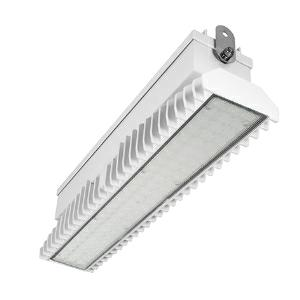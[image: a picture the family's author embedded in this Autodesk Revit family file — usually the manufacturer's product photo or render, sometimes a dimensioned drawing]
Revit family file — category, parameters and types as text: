
# Revit family: 3f_filippi_-_3f_lem_ampio_3f_filippi_-_58899_a0812_-_3f_lem_1_led_50_dali_cr_ampio___vs_c1d0
name_source: partatom
category: Lighting Fixtures
units: mm (PartAtom-declared; Revit-internal decimal feet)

## family parameters
Cut with Voids When Loaded = No
Host = Face
Light Source = No
Part Type = Normal
Room Calculation Point = No
Round Connector Dimension = Use Diameter
Shared = No

## types (1)
- 3F Filippi - 3F LEM Ampio (1 x LED, 6652 lm, 56 W, 4000 K)
    Apparent Load = 56 VA
    Approval mark = CE
    CIE Flux Codes = 67 90 97 100 100
    Color Rendering = 80
    Color Temperature = 4000 K
    Control Gear = Electronic transformer
    Default Elevation = 1800 mm
    Description = Industrial luminaire with high light output and high luminous efficiency designed with the most innovative technologies for environments with temperature up to 55°C.

ILLUMINOTECHNICAL
Luminous efficiency 100% (DLOR 98%, ULOR 2%).
Initial luminous flux of the luminaire 6652 lm.
Direct symmetric wide distribution: the illuminated area has a rectangular shape.
Installation Interdistance Transv.D = 1.24 x hu - Long.D = 1.20 x hu.
Tabular UGR (CIE 117 - 4H-8H; S=0.25H; 70/50/20): RUG 25.9 - 25.7.
Beam angle: 82° - 83°.
Luminous efficacy 119 lm/W.
Lifetime (L93/B10): 30000 h. (tq+25°C)
Lifetime (L90/B10): 50000 h. (tq+25°C)
Lifetime (L85/B10): 80000 h. (tq+25°C)
Lifetime (L80/B10): 100000 h. (tq+25°C)
Lifetime (L85/B10): 50000 h. (tq+55°C)
Sudden decreased luminous flux after 50000 hours: 0% (C0).
Photobiological safety in compliance with IEC/TR 62778: RG0 risk exempt, (IEC 62471).
In compliance with IEC/EN 62722-2-1 - IEC/EN 62717 standards.

SOURCE
Mid-Power linear LED module 50W/840.
Energy efficiency class (UE 2019/2020 - UE 2019/2015): C.
CIE 13.3 Colour rendering index: CRI >80 (R9 <50%).
IES TM-30 Fidelity Index: Rf = 84 Rg = 95.
CCT nominal colour temperature 4000 K.
Colour initial tolerance (MacAdam): SDCM 3.

MECHANICAL
Passive modular heatsinks in die-casted aluminium, painted in white colour.
To optimize the thermal management of the LED module, the heatsinks are oversized and provided with self-cleaning of cooling fins.
Wiring body in aluminium and galvanised steel anchored solidly to the sinks and thermally separated.
3F Lens lenses with high luminous efficiency, transparent methacrylate (PMMA), fixed to the LED modules.
Fixing brackets in stainless steel.
Luminaire with limited surface temperature. - D - (EN 60598-2-24)
Dimensions: 542x115 mm, height 154 mm. Weight 6.76 kg.
IP65 protection degree.
Mechanical strength to impacts IK06 (1 joule).
Glow-wire test resistance 650°C.

ELECTRICAL
Halogen Free DALI-2 DATI (Parts 251, 252, 253), PUSH-DIM, electronic wiring 230V-50/60Hz, power factor 0.95 at full load, THD <25%, constant output current, class I, 1 driver, 1 DALI addresse.
Power of the luminaire 56 W.
ENEC - CE.
SAFE FLICKER: PstLM=<1 and SVM=<0.4 (IEC TR 61547-1 and IEC TR 63158), to ensure a more comfortable and safe light.
Luminaire compliant with EN 60598-2-22 for power supply from a centralised emergency system CPSS (Central Power Supply System), not incorporated in the luminaire - high risk areas excluded. The default power and flux are 100% in AC and 15% in DC.
Ambient temperature from -30°C to +55°C.
Temperature class T6 max 85°C.
Quick connection via M25 5P connector with 9-13 mm tightening range.
Power unit positioned on a separate compartment by the LED module to ensure optimum temperatures of cabling components, to be inspectable and maintainable.
Relative humidity UR: <85%.

INSTALLATION
Ceiling / Suspended / Wall.
All accessories dedicated to this product are available on the Catalog and on our website www.3F-Filippi.com.

ACCESSORIES
A0812 - Anti-glare microprismatic VS moulded glass, tempered, not flammable, with sealing gasket.
One required for each light module. The pack contains 10 pieces.

APPLICATIONS
In commercial environments, exhibition and industrial areas, stores, open areas.
Applications with high ambient temperature up to 55°C.
Environments in which it is necessary a total protection against falling fragments (eg environments with foodstuffs or machines with moving parts or with extreme temperature changes), use luminaires with polycarbonate lenses.

LIGHT MANAGEMENT
Recommended minimum setting: 10%.
The luminaire, equipped with (DALI-2 DATI) driver, can be controlled manually with 3F Easy Dim technology or automatically/manually with wired or wireless DALI/D2D control systems.
The D2D driver guarantees interoperability with other devices with the same certification by making the following information available:
Device Data (Part 251), Energy Report (Part 252), Diagnosis & Maintenance (Part 253).
In electrical systems without a regulation system (manual or automatic) and DALI bus, a suitable jumper must be made on the DA-DA terminals of the appliance.

WARNING
Fixture not suitable for cold stores with an ambient temperature <0°C and/or relative humidity >85%.
Luminaire designed for disposal/recycling at end-of-life.
Replaceable (LED only) light source by a professional. Replaceable control gear by a professional.
    Height = 154 mm
    Lamp = 1 x LED
    Lamp Light Flux = 6652 lm
    Lamp Power = 56 W
    Lamp count = 1
    Length = 542 mm
    Lifetime = 50000 h
    Luminous efficacy = 119 lm/W
    Manufacturer = 3F Filippi
    ModVariant = No
    Model = 3F Filippi - 58899+A0812 - 3F LEM 1 LED 50 DALI CR AMPIO + VS
    Mounting Place = Ceiling
    Mounting Type = Pendant
    Number of Poles = 1
    OnlyDefault = Yes
    Power Factor = 1
    Product Name = 3F Filippi - 3F LEM Ampio
    Product group = pendant luminaire
    ProductGroupID = 9
    Protection Class = Protection class I
    Protection Degree = IP 65
    RLX_Detail_Level = 1
    RLX_Emergency_Light_Flux = 0 lm
    RLX_Emergency_Type = 0
    RLX_Emergency_Type_DB = No
    RlxData = <blob elided: 92761 chars, md5=74c45d42>
    Socket = socket
    Standby Power = 0 W
    System Light Flux = 6652 lm
    System Power = 56 W
    Type Comments = Product without accessories
    Type Image = 3f_filippi_-_lem_1__a0812.jpg
    URL = http://relux.com
    VarID = ---
    Voltage = 0 V
    Weight = 0.00 kg
    Width = 115 mm

## geometry (parser evidence)
native form markers: Blend x4, Sweep x13
no freeform markers — native parametric forms only
